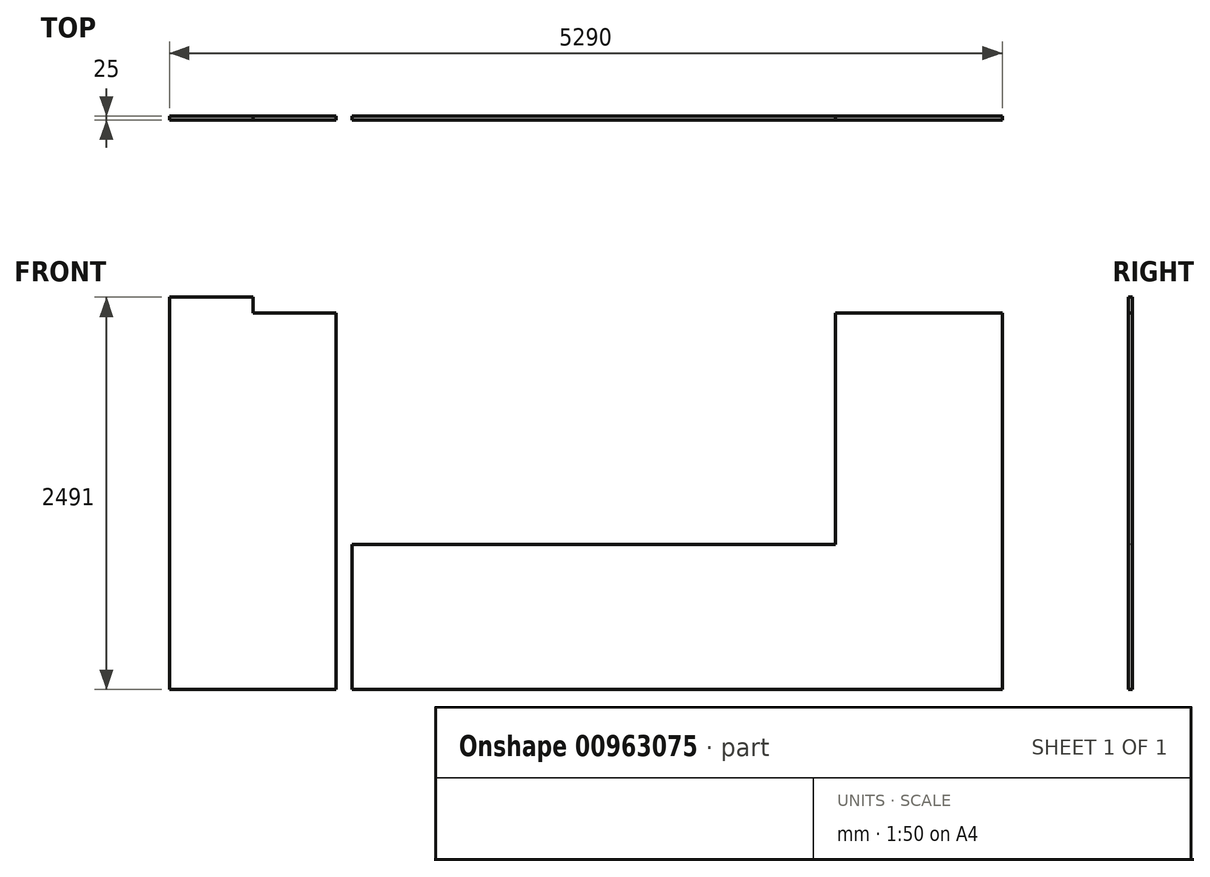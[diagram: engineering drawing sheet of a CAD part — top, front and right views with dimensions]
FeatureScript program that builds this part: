
annotation { "Feature Type Name" : "Feature", "Feature Type Description" : "" }
export const myFeature = defineFeature(function(context is Context, id is Id, definition is map)
    precondition{}
    {
        {
            var Q0;
            Q0=qCreatedBy(makeId("Front.planeOp"),FACE);
            var sketch = newSketch(context, id + "F0", { "sketchPlane" : qUnion([Q0])});
            skLineSegment(sketch, "E0.bottom", {"start": v(-2801.22, -1613.23) * mm, "end": v(2488.78, -1613.23) * mm});
            skLineSegment(sketch, "E0.top", {"start": v(-2801.22, 2186.77) * mm, "end": v(2488.78, 2186.77) * mm});
            skLineSegment(sketch, "E0.left", {"start": v(-2801.22, -1613.23) * mm, "end": v(-2801.22, 2186.77) * mm});
            skLineSegment(sketch, "E0.right", {"start": v(2488.78, -1613.23) * mm, "end": v(2488.78, 2186.77) * mm});
            skLineSegment(sketch, "E1.bottom", {"start": v(-2801.22, -1613.23) * mm, "end": v(-1741.22, -1613.23) * mm});
            skLineSegment(sketch, "E1.top", {"start": v(-2801.22, 777.77) * mm, "end": v(-1741.22, 777.77) * mm});
            skLineSegment(sketch, "E1.left", {"start": v(-2801.22, -1613.23) * mm, "end": v(-2801.22, 777.77) * mm});
            skLineSegment(sketch, "E1.right", {"start": v(-1741.22, -1613.23) * mm, "end": v(-1741.22, 777.77) * mm});
            skLineSegment(sketch, "E2.bottom", {"start": v(-2801.22, -1613.23) * mm, "end": v(-1641.22, -1613.23) * mm});
            skLineSegment(sketch, "E2.top", {"start": v(-2801.22, 877.77) * mm, "end": v(-1641.22, 877.77) * mm});
            skLineSegment(sketch, "E2.left", {"start": v(-2801.22, -1613.23) * mm, "end": v(-2801.22, 877.77) * mm});
            skLineSegment(sketch, "E2.right", {"start": v(-1641.22, -1613.23) * mm, "end": v(-1641.22, 877.77) * mm});
            skLineSegment(sketch, "E3.bottom", {"start": v(2488.78, -1613.23) * mm, "end": v(1428.78, -1613.23) * mm});
            skLineSegment(sketch, "E3.top", {"start": v(2488.78, 777.77) * mm, "end": v(1428.78, 777.77) * mm});
            skLineSegment(sketch, "E3.left", {"start": v(2488.78, -1613.23) * mm, "end": v(2488.78, 777.77) * mm});
            skLineSegment(sketch, "E3.right", {"start": v(1428.78, -1613.23) * mm, "end": v(1428.78, 777.77) * mm});
            skLineSegment(sketch, "E4", {"start": v(-1641.22, -693.23) * mm, "end": v(1428.78, -693.23) * mm});
            skLineSegment(sketch, "E5", {"start": v(-1641.22, -693.23) * mm, "end": v(2488.78, -693.23) * mm});
            skCircle(sketch, "E6", {"center": v(-2271.22, 1534.77) * mm, "radius": 90 * mm});
            skCircle(sketch, "E7", {"center": v(1958.78, 1533.73) * mm, "radius": 90 * mm});
            skLineSegment(sketch, "E8", {"start": v(-2271.22, 1444.77) * mm, "end": v(-2271.22, -1613.23) * mm});
            skLineSegment(sketch, "E9", {"start": v(1972.48, 1444.77) * mm, "end": v(1972.48, -1613.23) * mm});
            skLineSegment(sketch, "E10", {"start": v(-2271.22, 1534.77) * mm, "end": v(-2801.22, 1534.77) * mm});
            skSolve(sketch);
        }
        {
            var Q0;
            {var subQ5=sQuery(id+"F0.wireOp",EDGE,"E1.top");Q0=makeQuery(id+"F0.imprint","IMPRINT",FACE,{"disambiguationData":[TD([[makeQuery(id+"F0.imprint","IMPRINT",EDGE,{"derivedFrom":subQ5}),1.0]])]});}
            var Q1;
            {var subQ0=sQuery(id+"F0.wireOp",EDGE,"E0.bottom");Q1=makeQuery(id+"F0.imprint","IMPRINT",FACE,{"disambiguationData":[TD([[makeQuery(id+"F0.imprint","IMPRINT",EDGE,{"derivedFrom":subQ0}),1.0]])]});}
            var Q2;
            {var subQ0=sQuery(id+"F0.wireOp",EDGE,"E3.top");Q2=makeQuery(id+"F0.imprint","IMPRINT",FACE,{"disambiguationData":[TD([[makeQuery(id+"F0.imprint","IMPRINT",EDGE,{"derivedFrom":subQ0}),1.0]])]});}
            var Q3;
            {var subQ0=sQuery(id+"F0.wireOp",EDGE,"E3.bottom");Q3=makeQuery(id+"F0.imprint","IMPRINT",FACE,{"disambiguationData":[TD([[makeQuery(id+"F0.imprint","IMPRINT",EDGE,{"derivedFrom":subQ0}),-1.0]])]});}
            extrude(context, id + "F1", {"entities" : qUnion([Q0, Q1, Q2, Q3]), "oppositeDirection" : true, "depth" : 25 * mm, "offsetDistance" : 25 * mm});
        }
    });
